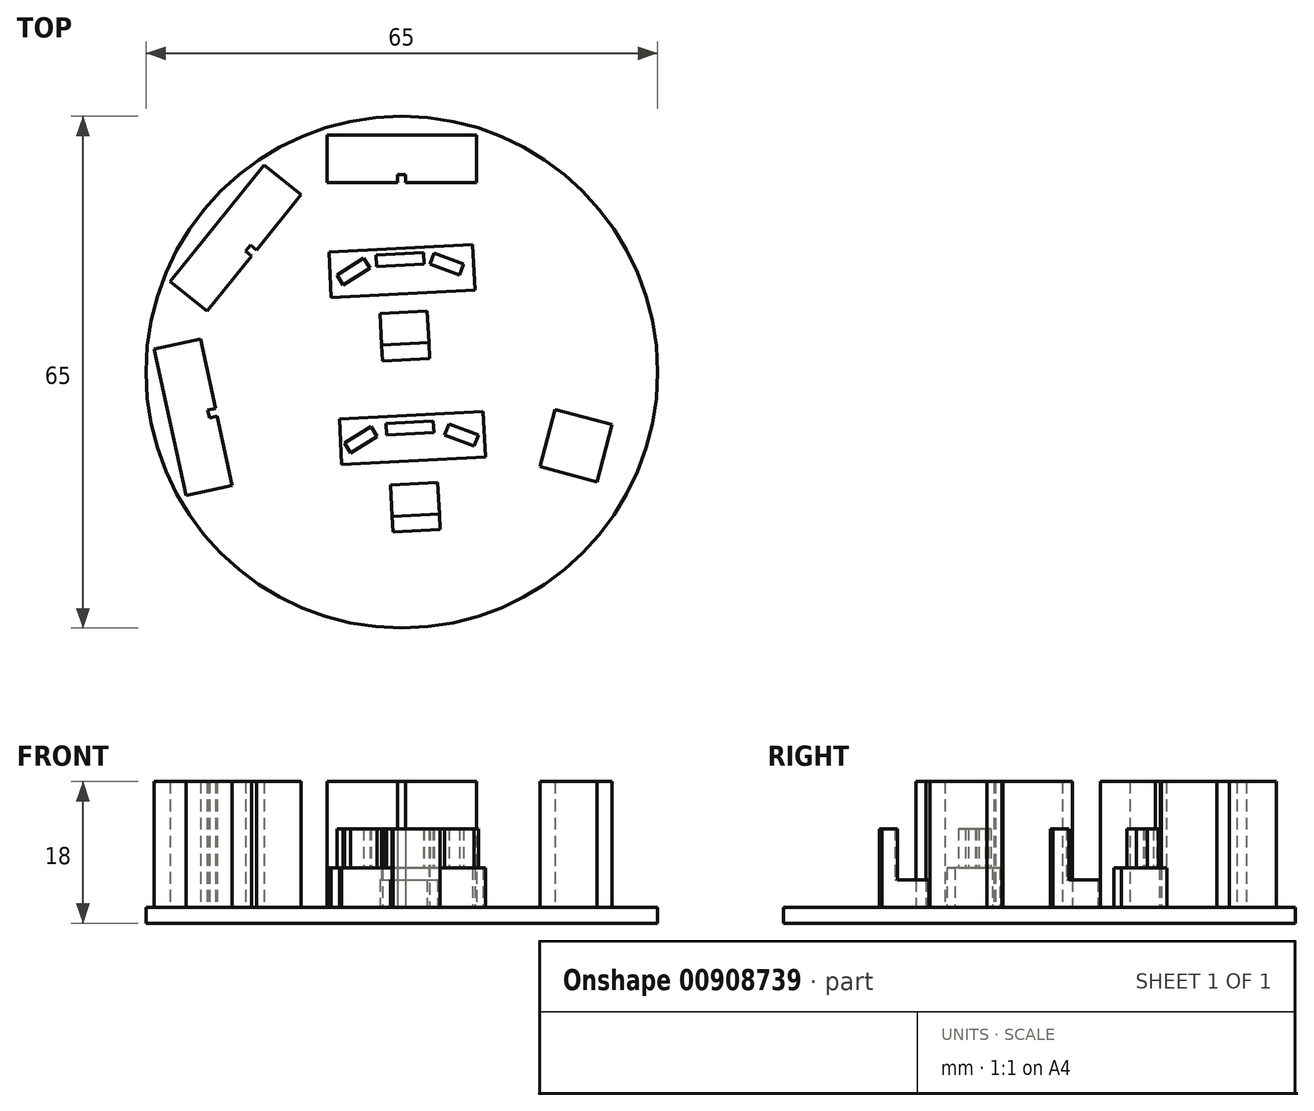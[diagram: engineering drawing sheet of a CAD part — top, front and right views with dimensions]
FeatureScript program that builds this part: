
annotation { "Feature Type Name" : "Feature", "Feature Type Description" : "" }
export const myFeature = defineFeature(function(context is Context, id is Id, definition is map)
    precondition{}
    {
        {
            var Q0;
            Q0=qCreatedBy(makeId("Top.planeOp"),FACE);
            var sketch = newSketch(context, id + "F0", { "sketchPlane" : qUnion([Q0])});
            skCircle(sketch, "E0", {"center": v(0, 0) * mm, "radius": 32.5 * mm});
            skSolve(sketch);
        }
        {
            var Q0;
            Q0 = qSketchRegion(id + "F0", true);
            extrude(context, id + "F1", {"entities" : qUnion([Q0]), "depth" : 2 * mm, "offsetDistance" : 25 * mm});
        }
        {
            var Q0;
            Q0=makeQuery(id+"F1.opExtrude","CAP_FACE",FACE,{"disambiguationData":[OSD([sQuery(id+"F0.wireOp",EDGE,"E0")])],"isStart":false});
            var sketch = newSketch(context, id + "F2", { "sketchPlane" : qUnion([Q0])});
            skLineSegment(sketch, "E1.top", {"start": v(-9.5, 30.1) * mm, "end": v(9.5, 30.1) * mm});
            skLineSegment(sketch, "E1.left", {"start": v(-9.5, 24.1) * mm, "end": v(-9.5, 30.1) * mm});
            skLineSegment(sketch, "E1.right", {"start": v(9.5, 24.1) * mm, "end": v(9.5, 30.1) * mm});
            skLineSegment(sketch, "E2", {"start": v(0, 0) * mm, "end": v(0, 32.5) * mm, "construction": true});
            skPoint(sketch, "E3", {"position": v(0, 24.1) * mm});
            skPoint(sketch, "E4.center", {"position": v(0, 0) * mm});
            skLineSegment(sketch, "E5", {"start": v(-0.5, 24.1) * mm, "end": v(-0.5, 25.1) * mm});
            skLineSegment(sketch, "E6", {"start": v(-0.5, 25.1) * mm, "end": v(0.5, 25.1) * mm});
            skLineSegment(sketch, "E7", {"start": v(0.5, 25.1) * mm, "end": v(0.5, 24.1) * mm});
            skLineSegment(sketch, "E8.trimOffspring", {"start": v(0.5, 24.1) * mm, "end": v(9.5, 24.1) * mm});
            skLineSegment(sketch, "E9", {"start": v(-0.5, 24.1) * mm, "end": v(-9.5, 24.1) * mm});
            skLineSegment(sketch, "E10.1.0", {"start": v(-29.4, 11.5) * mm, "end": v(-17.47, 26.3) * mm});
            skLineSegment(sketch, "E10.1.1", {"start": v(-24.73, 7.74) * mm, "end": v(-29.4, 11.5) * mm});
            skLineSegment(sketch, "E10.1.2", {"start": v(-19.08, 14.74) * mm, "end": v(-24.73, 7.74) * mm});
            skLineSegment(sketch, "E10.1.3", {"start": v(-19.08, 14.74) * mm, "end": v(-19.86, 15.37) * mm});
            skLineSegment(sketch, "E10.1.4", {"start": v(-19.86, 15.37) * mm, "end": v(-19.23, 16.15) * mm});
            skLineSegment(sketch, "E10.1.5", {"start": v(-19.23, 16.15) * mm, "end": v(-18.45, 15.52) * mm});
            skLineSegment(sketch, "E10.1.6", {"start": v(-18.45, 15.52) * mm, "end": v(-12.8, 22.53) * mm});
            skLineSegment(sketch, "E10.1.7", {"start": v(-12.8, 22.53) * mm, "end": v(-17.47, 26.3) * mm});
            skLineSegment(sketch, "E10.2.0", {"start": v(-27.4, -15.66) * mm, "end": v(-31.43, 2.9) * mm});
            skLineSegment(sketch, "E10.2.1", {"start": v(-21.55, -14.4) * mm, "end": v(-27.4, -15.66) * mm});
            skLineSegment(sketch, "E10.2.2", {"start": v(-23.45, -5.6) * mm, "end": v(-21.55, -14.4) * mm});
            skLineSegment(sketch, "E10.2.3", {"start": v(-23.45, -5.6) * mm, "end": v(-24.43, -5.8) * mm});
            skLineSegment(sketch, "E10.2.4", {"start": v(-24.43, -5.8) * mm, "end": v(-24.64, -4.83) * mm});
            skLineSegment(sketch, "E10.2.5", {"start": v(-24.64, -4.83) * mm, "end": v(-23.66, -4.62) * mm});
            skLineSegment(sketch, "E10.2.6", {"start": v(-23.66, -4.62) * mm, "end": v(-25.57, 4.18) * mm});
            skLineSegment(sketch, "E10.2.7", {"start": v(-25.57, 4.18) * mm, "end": v(-31.43, 2.9) * mm});
            skLineSegment(sketch, "E10.anchor1", {"start": v(0, 0) * mm, "end": v(-9.5, 30.1) * mm, "construction": true});
            skLineSegment(sketch, "E10.anchor2", {"start": v(0, 0) * mm, "end": v(-27.4, -15.66) * mm, "construction": true});
            skLineSegment(sketch, "E11.bottom", {"start": v(19.5, -4.74) * mm, "end": v(26.73, -6.68) * mm});
            skLineSegment(sketch, "E11.top", {"start": v(17.55, -11.98) * mm, "end": v(24.8, -13.92) * mm});
            skLineSegment(sketch, "E11.left", {"start": v(19.5, -4.74) * mm, "end": v(17.55, -11.98) * mm});
            skLineSegment(sketch, "E11.right", {"start": v(26.73, -6.68) * mm, "end": v(24.8, -13.92) * mm});
            skSolve(sketch);
        }
        {
            var Q0;
            Q0=makeQuery(id+"F2.imprint","IMPRINT",FACE,{"disambiguationData":[TD([[makeQuery(id+"F2.imprint","IMPRINT",EDGE,{"derivedFrom":sQuery(id+"F2.wireOp",EDGE,"E10.1.0")}),-1.0]])]});
            var Q1;
            Q1=makeQuery(id+"F2.imprint","IMPRINT",FACE,{"disambiguationData":[TD([[makeQuery(id+"F2.imprint","IMPRINT",EDGE,{"derivedFrom":sQuery(id+"F2.wireOp",EDGE,"E1.top")}),-1.0]])]});
            var Q2;
            Q2=makeQuery(id+"F2.imprint","IMPRINT",FACE,{"disambiguationData":[TD([[makeQuery(id+"F2.imprint","IMPRINT",EDGE,{"derivedFrom":sQuery(id+"F2.wireOp",EDGE,"E10.2.0")}),-1.0]])]});
            var Q3;
            Q3=makeQuery(id+"F2.imprint","IMPRINT",FACE,{"disambiguationData":[TD([[makeQuery(id+"F2.imprint","IMPRINT",EDGE,{"derivedFrom":sQuery(id+"F2.wireOp",EDGE,"E11.bottom")}),-1.0]])]});
            extrude(context, id + "F3", {"entities" : qUnion([Q0, Q1, Q2, Q3]), "operationType" : NewBodyOperationType.ADD, "depth" : 16 * mm, "offsetDistance" : 25 * mm});
        }
        {
            var Q0;
            Q0=makeQuery(id+"F1.opExtrude","CAP_FACE",FACE,{"disambiguationData":[OSD([sQuery(id+"F0.wireOp",EDGE,"E0")])],"isStart":false});
            var sketch = newSketch(context, id + "F4", { "sketchPlane" : qUnion([Q0])});
            skLineSegment(sketch, "E12.bottom", {"start": v(-9.25, 15.24) * mm, "end": v(9.02, 16.2) * mm});
            skLineSegment(sketch, "E12.top", {"start": v(-8.94, 9.47) * mm, "end": v(9.32, 10.43) * mm});
            skLineSegment(sketch, "E12.left", {"start": v(-9.25, 15.24) * mm, "end": v(-8.94, 9.47) * mm});
            skLineSegment(sketch, "E12.right", {"start": v(9.02, 16.2) * mm, "end": v(9.32, 10.43) * mm});
            skLineSegment(sketch, "E13.bottom", {"start": v(-7.93, -5.94) * mm, "end": v(10.34, -4.99) * mm});
            skLineSegment(sketch, "E13.top", {"start": v(-7.62, -11.72) * mm, "end": v(10.64, -10.76) * mm});
            skLineSegment(sketch, "E13.left", {"start": v(-7.93, -5.94) * mm, "end": v(-7.62, -11.72) * mm});
            skLineSegment(sketch, "E13.right", {"start": v(10.34, -4.99) * mm, "end": v(10.64, -10.76) * mm});
            skSolve(sketch);
        }
        {
            var Q0;
            Q0=makeQuery(id+"F4.imprint","IMPRINT",FACE,{"disambiguationData":[TD([[makeQuery(id+"F4.imprint","IMPRINT",EDGE,{"derivedFrom":sQuery(id+"F4.wireOp",EDGE,"E13.bottom")}),-1.0]])]});
            var Q1;
            Q1=makeQuery(id+"F4.imprint","IMPRINT",FACE,{"disambiguationData":[TD([[makeQuery(id+"F4.imprint","IMPRINT",EDGE,{"derivedFrom":sQuery(id+"F4.wireOp",EDGE,"E12.bottom")}),-1.0]])]});
            extrude(context, id + "F5", {"entities" : qUnion([Q0, Q1]), "operationType" : NewBodyOperationType.ADD, "depth" : 5 * mm, "offsetDistance" : 25 * mm});
        }
        {
            var Q0;
            Q0=makeQuery(id+"F1.opExtrude","CAP_FACE",FACE,{"disambiguationData":[OSD([sQuery(id+"F0.wireOp",EDGE,"E0")])],"isStart":false});
            var sketch = newSketch(context, id + "F6", { "sketchPlane" : qUnion([Q0])});
            skSolve(sketch);
        }
        {
            var Q0;
            Q0=makeQuery(id+"F6.imprint","IMPRINT",FACE,{"disambiguationData":[TD([[makeQuery(id+"F6.imprint","IMPRINT",EDGE,{"derivedFrom":makeQuery(id+"F1.opExtrude","CAP_EDGE",EDGE,{"disambiguationData":[OSD([sQuery(id+"F0.wireOp",EDGE,"E0")])],"isStart":false})}),1.0]])]});
            var sketch = newSketch(context, id + "F7", { "sketchPlane" : qUnion([Q0])});
            skLineSegment(sketch, "E14", {"start": v(-2.75, 7.42) * mm, "end": v(3.24, 7.74) * mm});
            skLineSegment(sketch, "E15", {"start": v(3.24, 7.74) * mm, "end": v(3.56, 1.75) * mm});
            skLineSegment(sketch, "E16", {"start": v(3.56, 1.75) * mm, "end": v(-2.44, 1.43) * mm});
            skLineSegment(sketch, "E17", {"start": v(-2.44, 1.43) * mm, "end": v(-2.75, 7.42) * mm});
            skLineSegment(sketch, "E18", {"start": v(-1.41, -14.32) * mm, "end": v(4.58, -14.01) * mm});
            skLineSegment(sketch, "E19", {"start": v(4.58, -14.01) * mm, "end": v(4.9, -20) * mm});
            skLineSegment(sketch, "E20", {"start": v(4.9, -20) * mm, "end": v(-1.1, -20.32) * mm});
            skLineSegment(sketch, "E21", {"start": v(-1.1, -20.32) * mm, "end": v(-1.41, -14.32) * mm});
            skSolve(sketch);
        }
        {
            var Q0;
            Q0 = qSketchRegion(id + "F7", true);
            extrude(context, id + "F8", {"entities" : qUnion([Q0]), "operationType" : NewBodyOperationType.ADD, "depth" : 3.5 * mm, "offsetDistance" : 25 * mm});
        }
        {
            var Q0;
            Q0=makeQuery(id+"F8.opExtrude","CAP_FACE",FACE,{"disambiguationData":[OSD([sQuery(id+"F7.wireOp",EDGE,"E18"),sQuery(id+"F7.wireOp",EDGE,"E19"),sQuery(id+"F7.wireOp",EDGE,"E20"),sQuery(id+"F7.wireOp",EDGE,"E21")])],"isStart":false});
            var sketch = newSketch(context, id + "F9", { "sketchPlane" : qUnion([Q0])});
            skLineSegment(sketch, "E22.0.0", {"start": v(-2.75, 7.42) * mm, "end": v(-2.44, 1.43) * mm});
            skLineSegment(sketch, "E22.0.1", {"start": v(-2.44, 1.43) * mm, "end": v(3.56, 1.75) * mm});
            skLineSegment(sketch, "E22.0.2", {"start": v(3.56, 1.75) * mm, "end": v(3.24, 7.74) * mm});
            skLineSegment(sketch, "E22.0.3", {"start": v(3.24, 7.74) * mm, "end": v(-2.75, 7.42) * mm});
            skLineSegment(sketch, "E23.0.0", {"start": v(-1.41, -14.32) * mm, "end": v(-1.1, -20.32) * mm});
            skLineSegment(sketch, "E23.0.1", {"start": v(-1.1, -20.32) * mm, "end": v(4.9, -20) * mm});
            skLineSegment(sketch, "E23.0.2", {"start": v(4.9, -20) * mm, "end": v(4.58, -14.01) * mm});
            skLineSegment(sketch, "E23.0.3", {"start": v(4.58, -14.01) * mm, "end": v(-1.41, -14.32) * mm});
            skLineSegment(sketch, "E24", {"start": v(-1.2, -18.32) * mm, "end": v(4.79, -18) * mm});
            skLineSegment(sketch, "E25", {"start": v(-2.54, 3.43) * mm, "end": v(3.45, 3.74) * mm});
            skSolve(sketch);
        }
        {
            var Q0;
            {var subQ0=sQuery(id+"F9.wireOp",EDGE,"E22.0.1");Q0=makeQuery(id+"F9.imprint","IMPRINT",FACE,{"disambiguationData":[TD([[makeQuery(id+"F9.imprint","IMPRINT",EDGE,{"derivedFrom":subQ0}),1.0]])]});}
            var Q1;
            {var subQ0=sQuery(id+"F9.wireOp",EDGE,"E23.0.1");Q1=makeQuery(id+"F9.imprint","IMPRINT",FACE,{"disambiguationData":[TD([[makeQuery(id+"F9.imprint","IMPRINT",EDGE,{"derivedFrom":subQ0}),-1.0]])]});}
            extrude(context, id + "F10", {"entities" : qUnion([Q0, Q1]), "operationType" : NewBodyOperationType.ADD, "depth" : 6.5 * mm, "offsetDistance" : 25 * mm});
        }
        {
            var Q0;
            Q0=makeQuery(id+"F5.opExtrude","CAP_FACE",FACE,{"disambiguationData":[OSD([sQuery(id+"F4.wireOp",EDGE,"E13.bottom"),sQuery(id+"F4.wireOp",EDGE,"E13.top"),sQuery(id+"F4.wireOp",EDGE,"E13.left"),sQuery(id+"F4.wireOp",EDGE,"E13.right")])],"isStart":false});
            var sketch = newSketch(context, id + "F11", { "sketchPlane" : qUnion([Q0])});
            skLineSegment(sketch, "E26.0.0", {"start": v(-7.93, -5.94) * mm, "end": v(-7.62, -11.72) * mm});
            skLineSegment(sketch, "E26.0.1", {"start": v(-7.62, -11.72) * mm, "end": v(10.64, -10.76) * mm});
            skLineSegment(sketch, "E26.0.2", {"start": v(10.64, -10.76) * mm, "end": v(10.34, -4.99) * mm});
            skLineSegment(sketch, "E26.0.3", {"start": v(10.34, -4.99) * mm, "end": v(-7.93, -5.94) * mm});
            skLineSegment(sketch, "E27.0.0", {"start": v(-9.25, 15.24) * mm, "end": v(-8.94, 9.47) * mm});
            skLineSegment(sketch, "E27.0.1", {"start": v(-8.94, 9.47) * mm, "end": v(9.32, 10.43) * mm});
            skLineSegment(sketch, "E27.0.2", {"start": v(9.32, 10.43) * mm, "end": v(9.02, 16.2) * mm});
            skLineSegment(sketch, "E27.0.3", {"start": v(9.02, 16.2) * mm, "end": v(-9.25, 15.24) * mm});
            skLineSegment(sketch, "E28", {"start": v(-8.22, 12.36) * mm, "end": v(-7.42, 11.09) * mm});
            skPoint(sketch, "E28.startSnap0", {"position": v(-9.1, 12.36) * mm});
            skLineSegment(sketch, "E29", {"start": v(-7.42, 11.09) * mm, "end": v(-4.03, 13.21) * mm});
            skLineSegment(sketch, "E30", {"start": v(-4.03, 13.21) * mm, "end": v(-4.83, 14.48) * mm});
            skLineSegment(sketch, "E31", {"start": v(-4.83, 14.48) * mm, "end": v(-8.22, 12.36) * mm});
            skLineSegment(sketch, "E32", {"start": v(-3.25, 14.9) * mm, "end": v(-3.17, 13.4) * mm});
            skLineSegment(sketch, "E33", {"start": v(-3.17, 13.4) * mm, "end": v(2.83, 13.72) * mm});
            skLineSegment(sketch, "E34", {"start": v(2.83, 13.72) * mm, "end": v(2.75, 15.22) * mm});
            skLineSegment(sketch, "E35", {"start": v(2.75, 15.22) * mm, "end": v(-3.25, 14.9) * mm});
            skLineSegment(sketch, "E36", {"start": v(4.13, 15.1) * mm, "end": v(3.61, 13.7) * mm});
            skLineSegment(sketch, "E37", {"start": v(3.61, 13.7) * mm, "end": v(7.36, 12.3) * mm});
            skLineSegment(sketch, "E38", {"start": v(7.36, 12.3) * mm, "end": v(7.88, 13.72) * mm});
            skLineSegment(sketch, "E39", {"start": v(7.88, 13.72) * mm, "end": v(4.13, 15.1) * mm});
            skLineSegment(sketch, "E40", {"start": v(-7.3, -9) * mm, "end": v(-6.5, -10.27) * mm});
            skLineSegment(sketch, "E41", {"start": v(-6.5, -10.27) * mm, "end": v(-3.1, -8.15) * mm});
            skLineSegment(sketch, "E42", {"start": v(-3.1, -8.15) * mm, "end": v(-3.9, -6.88) * mm});
            skLineSegment(sketch, "E43", {"start": v(-3.9, -6.88) * mm, "end": v(-7.3, -9) * mm});
            skLineSegment(sketch, "E44", {"start": v(-1.99, -6.5) * mm, "end": v(-1.9, -8) * mm});
            skLineSegment(sketch, "E45", {"start": v(-1.9, -8) * mm, "end": v(4.08, -7.68) * mm});
            skLineSegment(sketch, "E46", {"start": v(4.08, -7.68) * mm, "end": v(4, -6.18) * mm});
            skLineSegment(sketch, "E47", {"start": v(4, -6.18) * mm, "end": v(-1.99, -6.5) * mm});
            skLineSegment(sketch, "E48", {"start": v(5.98, -6.6) * mm, "end": v(5.46, -8) * mm});
            skLineSegment(sketch, "E49", {"start": v(5.46, -8) * mm, "end": v(9.2, -9.4) * mm});
            skLineSegment(sketch, "E50", {"start": v(9.2, -9.4) * mm, "end": v(9.73, -7.99) * mm});
            skLineSegment(sketch, "E51", {"start": v(9.73, -7.99) * mm, "end": v(5.98, -6.6) * mm});
            skSolve(sketch);
        }
        {
            var Q0;
            Q0=makeQuery(id+"F11.imprint","IMPRINT",FACE,{"disambiguationData":[TD([[makeQuery(id+"F11.imprint","IMPRINT",EDGE,{"derivedFrom":sQuery(id+"F11.wireOp",EDGE,"E40")}),1.0]])]});
            var Q1;
            Q1=makeQuery(id+"F11.imprint","IMPRINT",FACE,{"disambiguationData":[TD([[makeQuery(id+"F11.imprint","IMPRINT",EDGE,{"derivedFrom":sQuery(id+"F11.wireOp",EDGE,"E44")}),1.0]])]});
            var Q2;
            Q2=makeQuery(id+"F11.imprint","IMPRINT",FACE,{"disambiguationData":[TD([[makeQuery(id+"F11.imprint","IMPRINT",EDGE,{"derivedFrom":sQuery(id+"F11.wireOp",EDGE,"E48")}),1.0]])]});
            var Q3;
            Q3=makeQuery(id+"F11.imprint","IMPRINT",FACE,{"disambiguationData":[TD([[makeQuery(id+"F11.imprint","IMPRINT",EDGE,{"derivedFrom":sQuery(id+"F11.wireOp",EDGE,"E28")}),1.0]])]});
            var Q4;
            Q4=makeQuery(id+"F11.imprint","IMPRINT",FACE,{"disambiguationData":[TD([[makeQuery(id+"F11.imprint","IMPRINT",EDGE,{"derivedFrom":sQuery(id+"F11.wireOp",EDGE,"E32")}),1.0]])]});
            var Q5;
            Q5=makeQuery(id+"F11.imprint","IMPRINT",FACE,{"disambiguationData":[TD([[makeQuery(id+"F11.imprint","IMPRINT",EDGE,{"derivedFrom":sQuery(id+"F11.wireOp",EDGE,"E36")}),1.0]])]});
            extrude(context, id + "F12", {"entities" : qUnion([Q0, Q1, Q2, Q3, Q4, Q5]), "operationType" : NewBodyOperationType.ADD, "depth" : 5 * mm, "offsetDistance" : 25 * mm});
        }
    });
